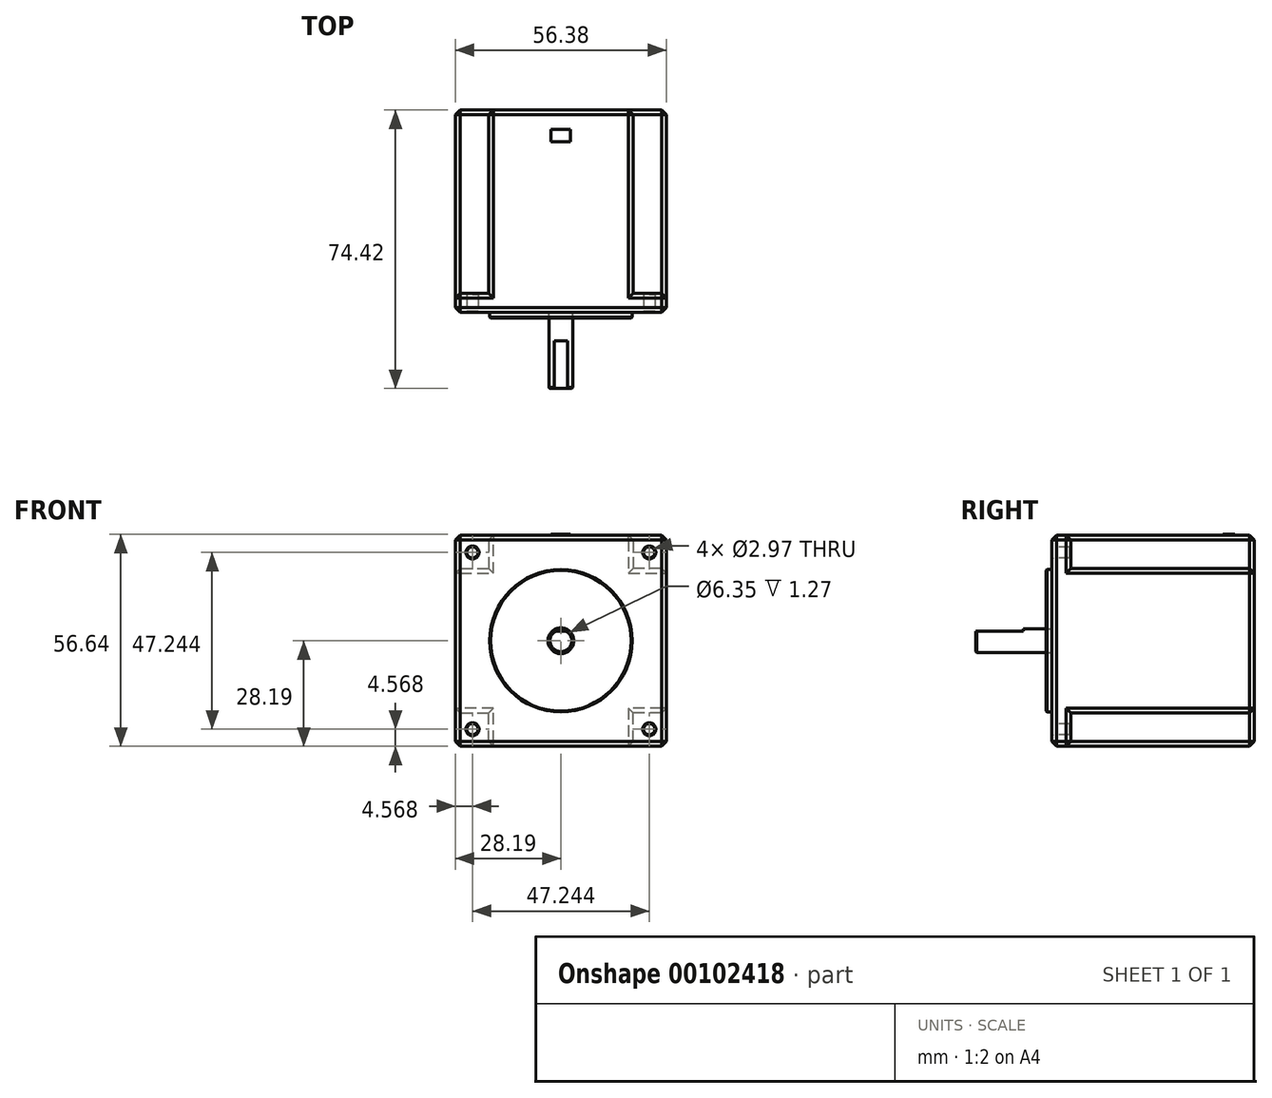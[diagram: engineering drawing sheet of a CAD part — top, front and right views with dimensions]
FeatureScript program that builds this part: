
annotation { "Feature Type Name" : "Feature", "Feature Type Description" : "" }
export const myFeature = defineFeature(function(context is Context, id is Id, definition is map)
    precondition{}
    {
        {
            var Q0;
            Q0=qCreatedBy(makeId("Front.planeOp"),FACE);
            var sketch = newSketch(context, id + "F0", { "sketchPlane" : qUnion([Q0]), "disableImprinting" : false});
            skCircle(sketch, "E0", {"center": v(0, 0) * mm, "radius": 19.05 * mm});
            skLineSegment(sketch, "E1.bottom", {"start": v(28.2, 28.2) * mm, "end": v(-28.2, 28.2) * mm});
            skLineSegment(sketch, "E1.top", {"start": v(28.2, -28.2) * mm, "end": v(-28.2, -28.2) * mm});
            skLineSegment(sketch, "E1.left", {"start": v(28.2, 28.2) * mm, "end": v(28.2, -28.2) * mm});
            skLineSegment(sketch, "E1.right", {"start": v(-28.2, 28.2) * mm, "end": v(-28.2, -28.2) * mm});
            skCircle(sketch, "E2", {"center": v(0, 0) * mm, "radius": 3.18 * mm});
            skCircle(sketch, "E3", {"center": v(-23.62, 23.62) * mm, "radius": 1.49 * mm});
            skCircle(sketch, "E4", {"center": v(23.62, 23.62) * mm, "radius": 1.49 * mm});
            skCircle(sketch, "E5", {"center": v(23.62, -23.62) * mm, "radius": 1.49 * mm});
            skCircle(sketch, "E6", {"center": v(-23.62, -23.62) * mm, "radius": 1.49 * mm});
            skLineSegment(sketch, "E7", {"start": v(-23.62, 23.62) * mm, "end": v(-23.62, 28.2) * mm, "construction": true});
            skLineSegment(sketch, "E8", {"start": v(-23.62, 28.2) * mm, "end": v(-23.62, 23.62) * mm, "construction": true});
            skLineSegment(sketch, "E9", {"start": v(-23.62, 23.62) * mm, "end": v(-28.2, 23.62) * mm, "construction": true});
            skLineSegment(sketch, "E10", {"start": v(23.62, 23.62) * mm, "end": v(23.62, 28.2) * mm, "construction": true});
            skLineSegment(sketch, "E11", {"start": v(23.62, 23.62) * mm, "end": v(28.2, 23.62) * mm, "construction": true});
            skLineSegment(sketch, "E12", {"start": v(23.62, -23.62) * mm, "end": v(28.2, -23.62) * mm, "construction": true});
            skLineSegment(sketch, "E13", {"start": v(23.62, -23.62) * mm, "end": v(23.62, -28.2) * mm, "construction": true});
            skLineSegment(sketch, "E14", {"start": v(-23.62, -23.62) * mm, "end": v(-23.62, -28.2) * mm, "construction": true});
            skLineSegment(sketch, "E15", {"start": v(-23.62, -23.62) * mm, "end": v(-28.2, -23.62) * mm, "construction": true});
            skSolve(sketch);
        }
        {
            var Q0;
            Q0 = qSketchRegion(id + "F0", true);
            var Q1;
            Q1=makeQuery(id+"F0.imprint","IMPRINT",FACE,{"disambiguationData":[TD([[makeQuery(id+"F0.imprint","IMPRINT",EDGE,{"derivedFrom":sQuery(id+"F0.wireOp",EDGE,"E0")}),1.0]])]});
            var Q2;
            Q2=makeQuery(id+"F0.imprint","IMPRINT",FACE,{"disambiguationData":[TD([[makeQuery(id+"F0.imprint","IMPRINT",EDGE,{"derivedFrom":sQuery(id+"F0.wireOp",EDGE,"E2")}),1.0]])]});
            extrude(context, id + "F1", {"entities" : qUnion([Q0, Q1, Q2]), "oppositeDirection" : true, "depth" : 54.1 * mm});
        }
        {
            var Q0;
            Q0=makeQuery(id+"F0.imprint","IMPRINT",FACE,{"disambiguationData":[TD([[makeQuery(id+"F0.imprint","IMPRINT",EDGE,{"derivedFrom":sQuery(id+"F0.wireOp",EDGE,"E0")}),1.0]])]});
            extrude(context, id + "F2", {"entities" : qUnion([Q0]), "operationType" : NewBodyOperationType.ADD, "depth" : 1.52 * mm});
        }
        {
            var Q0;
            Q0=makeQuery(id+"F0.imprint","IMPRINT",FACE,{"disambiguationData":[TD([[makeQuery(id+"F0.imprint","IMPRINT",EDGE,{"derivedFrom":sQuery(id+"F0.wireOp",EDGE,"E2")}),1.0]])]});
            extrude(context, id + "F3", {"entities" : qUnion([Q0]), "depth" : 20.32 * mm});
        }
        {
            var Q0;
            Q0=makeQuery(id+"F3.opExtrude","CAP_FACE",FACE,{"disambiguationData":[OSD([sQuery(id+"F0.wireOp",EDGE,"E2")])],"isStart":false});
            var sketch = newSketch(context, id + "F4", { "sketchPlane" : qUnion([Q0]), "disableImprinting" : false});
            skLineSegment(sketch, "E16", {"start": v(-1.8, 2.62) * mm, "end": v(1.8, 2.62) * mm});
            skSolve(sketch);
        }
        {
            var Q0;
            {var subQ0=sQuery(id+"F4.wireOp",EDGE,"E16");Q0=makeQuery(id+"F4.imprint","IMPRINT",FACE,{"disambiguationData":[TD([[makeQuery(id+"F4.imprint","IMPRINT",EDGE,{"derivedFrom":subQ0}),1.0]])]});}
            extrude(context, id + "F5", {"entities" : qUnion([Q0]), "operationType" : NewBodyOperationType.REMOVE, "oppositeDirection" : true, "depth" : 12.7 * mm});
        }
        {
            var Q0;
            Q0=makeQuery(id+"F1.opExtrude","CAP_FACE",FACE,{"disambiguationData":[OSD([sQuery(id+"F0.wireOp",EDGE,"E1.bottom"),sQuery(id+"F0.wireOp",EDGE,"E1.top"),sQuery(id+"F0.wireOp",EDGE,"E1.left"),sQuery(id+"F0.wireOp",EDGE,"E1.right"),sQuery(id+"F0.wireOp",EDGE,"E3"),sQuery(id+"F0.wireOp",EDGE,"E4"),sQuery(id+"F0.wireOp",EDGE,"E5"),sQuery(id+"F0.wireOp",EDGE,"E6")])],"isStart":false});
            var sketch = newSketch(context, id + "F6", { "sketchPlane" : qUnion([Q0])});
            skLineSegment(sketch, "E17.bottom", {"start": v(-28.2, 28.2) * mm, "end": v(-19.3, 28.2) * mm});
            skLineSegment(sketch, "E17.top", {"start": v(-28.2, 19.3) * mm, "end": v(-19.3, 19.3) * mm});
            skLineSegment(sketch, "E17.left", {"start": v(-28.2, 28.2) * mm, "end": v(-28.2, 19.3) * mm});
            skLineSegment(sketch, "E17.right", {"start": v(-19.3, 28.2) * mm, "end": v(-19.3, 19.3) * mm});
            skLineSegment(sketch, "E18.bottom", {"start": v(28.2, 28.2) * mm, "end": v(19.3, 28.2) * mm});
            skLineSegment(sketch, "E18.top", {"start": v(28.2, 19.3) * mm, "end": v(19.3, 19.3) * mm});
            skLineSegment(sketch, "E18.left", {"start": v(28.2, 28.2) * mm, "end": v(28.2, 19.3) * mm});
            skLineSegment(sketch, "E18.right", {"start": v(19.3, 28.2) * mm, "end": v(19.3, 19.3) * mm});
            skLineSegment(sketch, "E19.bottom", {"start": v(28.2, -28.2) * mm, "end": v(19.3, -28.2) * mm});
            skLineSegment(sketch, "E19.top", {"start": v(28.2, -19.3) * mm, "end": v(19.3, -19.3) * mm});
            skLineSegment(sketch, "E19.left", {"start": v(28.2, -28.2) * mm, "end": v(28.2, -19.3) * mm});
            skLineSegment(sketch, "E19.right", {"start": v(19.3, -28.2) * mm, "end": v(19.3, -19.3) * mm});
            skLineSegment(sketch, "E20.bottom", {"start": v(-28.2, -28.2) * mm, "end": v(-19.3, -28.2) * mm});
            skLineSegment(sketch, "E20.top", {"start": v(-28.2, -19.3) * mm, "end": v(-19.3, -19.3) * mm});
            skLineSegment(sketch, "E20.left", {"start": v(-28.2, -28.2) * mm, "end": v(-28.2, -19.3) * mm});
            skLineSegment(sketch, "E20.right", {"start": v(-19.3, -28.2) * mm, "end": v(-19.3, -19.3) * mm});
            skSolve(sketch);
        }
        {
            var Q0;
            Q0 = qSketchRegion(id + "F6", true);
            var Q1;
            {var subQ0=sQuery(id+"F0.wireOp",EDGE,"E1.right");var subQ1=sQuery(id+"F0.wireOp",EDGE,"E1.left");var subQ2=sQuery(id+"F0.wireOp",EDGE,"E1.top");var subQ3=sQuery(id+"F0.wireOp",EDGE,"E1.bottom");var subQ4=sQuery(id+"F0.wireOp",EDGE,"E3");var subQ5=sQuery(id+"F0.wireOp",EDGE,"E4");var subQ6=sQuery(id+"F0.wireOp",EDGE,"E5");var subQ7=sQuery(id+"F0.wireOp",EDGE,"E6");Q1=makeQuery(id+"F2.boolean.opBoolean","SPLIT",FACE,{"disambiguationData":[TD([makeQuery(id+"F1.opExtrude","SWEPT_FACE",FACE,{"disambiguationData":[OSD([subQ3])]})])],"derivedFrom":makeQuery(id+"F1.opExtrude","CAP_FACE",FACE,{"disambiguationData":[OSD([subQ3,subQ2,subQ1,subQ0,subQ4,subQ5,subQ6,subQ7])],"isStart":true})});}
            extrude(context, id + "F7", {"entities" : qUnion([Q0]), "operationType" : NewBodyOperationType.REMOVE, "oppositeDirection" : true, "endBoundEntityFace" : qUnion([Q1]), "depth" : 49.02 * mm});
        }
        {
            var Q0;
            Q0=makeQuery(id+"F1.opExtrude","SWEPT_FACE",FACE,{"disambiguationData":[OSD([sQuery(id+"F0.wireOp",EDGE,"E1.right")])]});
            var Q1;
            Q1=makeQuery(id+"F1.opExtrude","SWEPT_FACE",FACE,{"disambiguationData":[OSD([sQuery(id+"F0.wireOp",EDGE,"E1.bottom")])]});
            var Q2;
            Q2=makeQuery(id+"F1.opExtrude","SWEPT_FACE",FACE,{"disambiguationData":[OSD([sQuery(id+"F0.wireOp",EDGE,"E1.left")])]});
            var Q3;
            Q3=makeQuery(id+"F1.opExtrude","SWEPT_FACE",FACE,{"disambiguationData":[OSD([sQuery(id+"F0.wireOp",EDGE,"E1.top")])]});
            var Q4;
            Q4=makeQuery(id+"F1.opExtrude","CAP_FACE",FACE,{"disambiguationData":[OSD([sQuery(id+"F0.wireOp",EDGE,"E1.bottom"),sQuery(id+"F0.wireOp",EDGE,"E1.top"),sQuery(id+"F0.wireOp",EDGE,"E1.left"),sQuery(id+"F0.wireOp",EDGE,"E1.right"),sQuery(id+"F0.wireOp",EDGE,"E3"),sQuery(id+"F0.wireOp",EDGE,"E4"),sQuery(id+"F0.wireOp",EDGE,"E5"),sQuery(id+"F0.wireOp",EDGE,"E6")])],"isStart":false});
            chamfer(context, id + "F8", {"entities" : qUnion([Q0, Q1, Q2, Q3, Q4]), "width" : 1.27 * mm, "tangentPropagation" : true});
        }
        {
            var Q0;
            Q0=makeQuery(id+"F7.boolean.opBoolean","INTERSECT",EDGE,{"derivedFrom":[makeQuery(id+"F1.opExtrude","SWEPT_FACE",FACE,{"disambiguationData":[OSD([sQuery(id+"F0.wireOp",EDGE,"E3")])]}),makeQuery(id+"F7.opExtrude","CAP_FACE",FACE,{"disambiguationData":[OSD([sQuery(id+"F6.wireOp",EDGE,"E18.bottom"),sQuery(id+"F6.wireOp",EDGE,"E18.top"),sQuery(id+"F6.wireOp",EDGE,"E18.left"),sQuery(id+"F6.wireOp",EDGE,"E18.right")])],"isStart":false})]});
            var Q1;
            Q1=makeQuery(id+"F7.boolean.opBoolean","INTERSECT",EDGE,{"derivedFrom":[makeQuery(id+"F1.opExtrude","SWEPT_FACE",FACE,{"disambiguationData":[OSD([sQuery(id+"F0.wireOp",EDGE,"E6")])]}),makeQuery(id+"F7.opExtrude","CAP_FACE",FACE,{"disambiguationData":[OSD([sQuery(id+"F6.wireOp",EDGE,"E19.bottom"),sQuery(id+"F6.wireOp",EDGE,"E19.top"),sQuery(id+"F6.wireOp",EDGE,"E19.left"),sQuery(id+"F6.wireOp",EDGE,"E19.right")])],"isStart":false})]});
            var Q2;
            Q2=makeQuery(id+"F7.boolean.opBoolean","INTERSECT",EDGE,{"derivedFrom":[makeQuery(id+"F1.opExtrude","SWEPT_FACE",FACE,{"disambiguationData":[OSD([sQuery(id+"F0.wireOp",EDGE,"E4")])]}),makeQuery(id+"F7.opExtrude","CAP_FACE",FACE,{"disambiguationData":[OSD([sQuery(id+"F6.wireOp",EDGE,"E17.bottom"),sQuery(id+"F6.wireOp",EDGE,"E17.top"),sQuery(id+"F6.wireOp",EDGE,"E17.left"),sQuery(id+"F6.wireOp",EDGE,"E17.right")])],"isStart":false})]});
            var Q3;
            Q3=makeQuery(id+"F7.boolean.opBoolean","INTERSECT",EDGE,{"derivedFrom":[makeQuery(id+"F1.opExtrude","SWEPT_FACE",FACE,{"disambiguationData":[OSD([sQuery(id+"F0.wireOp",EDGE,"E5")])]}),makeQuery(id+"F7.opExtrude","CAP_FACE",FACE,{"disambiguationData":[OSD([sQuery(id+"F6.wireOp",EDGE,"E20.bottom"),sQuery(id+"F6.wireOp",EDGE,"E20.top"),sQuery(id+"F6.wireOp",EDGE,"E20.left"),sQuery(id+"F6.wireOp",EDGE,"E20.right")])],"isStart":false})]});
            var Q4;
            Q4=makeQuery(id+"F1.opExtrude","CAP_EDGE",EDGE,{"disambiguationData":[OSD([sQuery(id+"F0.wireOp",EDGE,"E5")])],"isStart":true});
            var Q5;
            Q5=makeQuery(id+"F1.opExtrude","CAP_EDGE",EDGE,{"disambiguationData":[OSD([sQuery(id+"F0.wireOp",EDGE,"E4")])],"isStart":true});
            var Q6;
            Q6=makeQuery(id+"F1.opExtrude","CAP_EDGE",EDGE,{"disambiguationData":[OSD([sQuery(id+"F0.wireOp",EDGE,"E3")])],"isStart":true});
            var Q7;
            Q7=makeQuery(id+"F1.opExtrude","CAP_EDGE",EDGE,{"disambiguationData":[OSD([sQuery(id+"F0.wireOp",EDGE,"E6")])],"isStart":true});
            var Q8;
            Q8=makeQuery(id+"F2.opExtrude","CAP_EDGE",EDGE,{"disambiguationData":[OSD([sQuery(id+"F0.wireOp",EDGE,"E0")])],"isStart":true});
            var Q9;
            Q9=makeQuery(id+"F2.opExtrude","CAP_EDGE",EDGE,{"disambiguationData":[OSD([sQuery(id+"F0.wireOp",EDGE,"E0")])],"isStart":false});
            var Q10;
            Q10=makeQuery(id+"F3.opExtrude","CAP_EDGE",EDGE,{"disambiguationData":[OSD([sQuery(id+"F0.wireOp",EDGE,"E2")])],"isStart":false});
            var Q11;
            Q11=makeQuery(id+"F5.boolean.opBoolean","COPY",EDGE,{"derivedFrom":makeQuery(id+"F5.opExtrude","CAP_EDGE",EDGE,{"disambiguationData":[OSD([sQuery(id+"F4.wireOp",EDGE,"E16")])],"isStart":true})});
            var Q12;
            Q12=makeQuery(id+"F2.opExtrude","CAP_EDGE",EDGE,{"disambiguationData":[OSD([sQuery(id+"F0.wireOp",EDGE,"E2")])],"isStart":false});
            chamfer(context, id + "F9", {"entities" : qUnion([Q0, Q1, Q2, Q3, Q4, Q5, Q6, Q7, Q8, Q9, Q10, Q11, Q12]), "width" : 0.25 * mm, "tangentPropagation" : true});
        }
        {
            var Q0;
            Q0=makeQuery(id+"F1.opExtrude","SWEPT_FACE",FACE,{"disambiguationData":[OSD([sQuery(id+"F0.wireOp",EDGE,"E1.bottom")])]});
            var sketch = newSketch(context, id + "F10", { "sketchPlane" : qUnion([Q0])});
            skLineSegment(sketch, "E21.bottom", {"start": v(2.6, 48.9) * mm, "end": v(-2.6, 48.9) * mm});
            skLineSegment(sketch, "E21.top", {"start": v(2.6, 45.63) * mm, "end": v(-2.6, 45.63) * mm});
            skLineSegment(sketch, "E21.left", {"start": v(2.6, 48.9) * mm, "end": v(2.6, 45.63) * mm});
            skLineSegment(sketch, "E21.right", {"start": v(-2.6, 48.9) * mm, "end": v(-2.6, 45.63) * mm});
            skPoint(sketch, "E21.middle", {"position": v(0, 47.26) * mm});
            skSolve(sketch);
        }
        {
            var Q0;
            Q0 = qSketchRegion(id + "F10", true);
            extrude(context, id + "F11", {"entities" : qUnion([Q0]), "operationType" : NewBodyOperationType.ADD, "depth" : 0.25 * mm});
        }
    });
